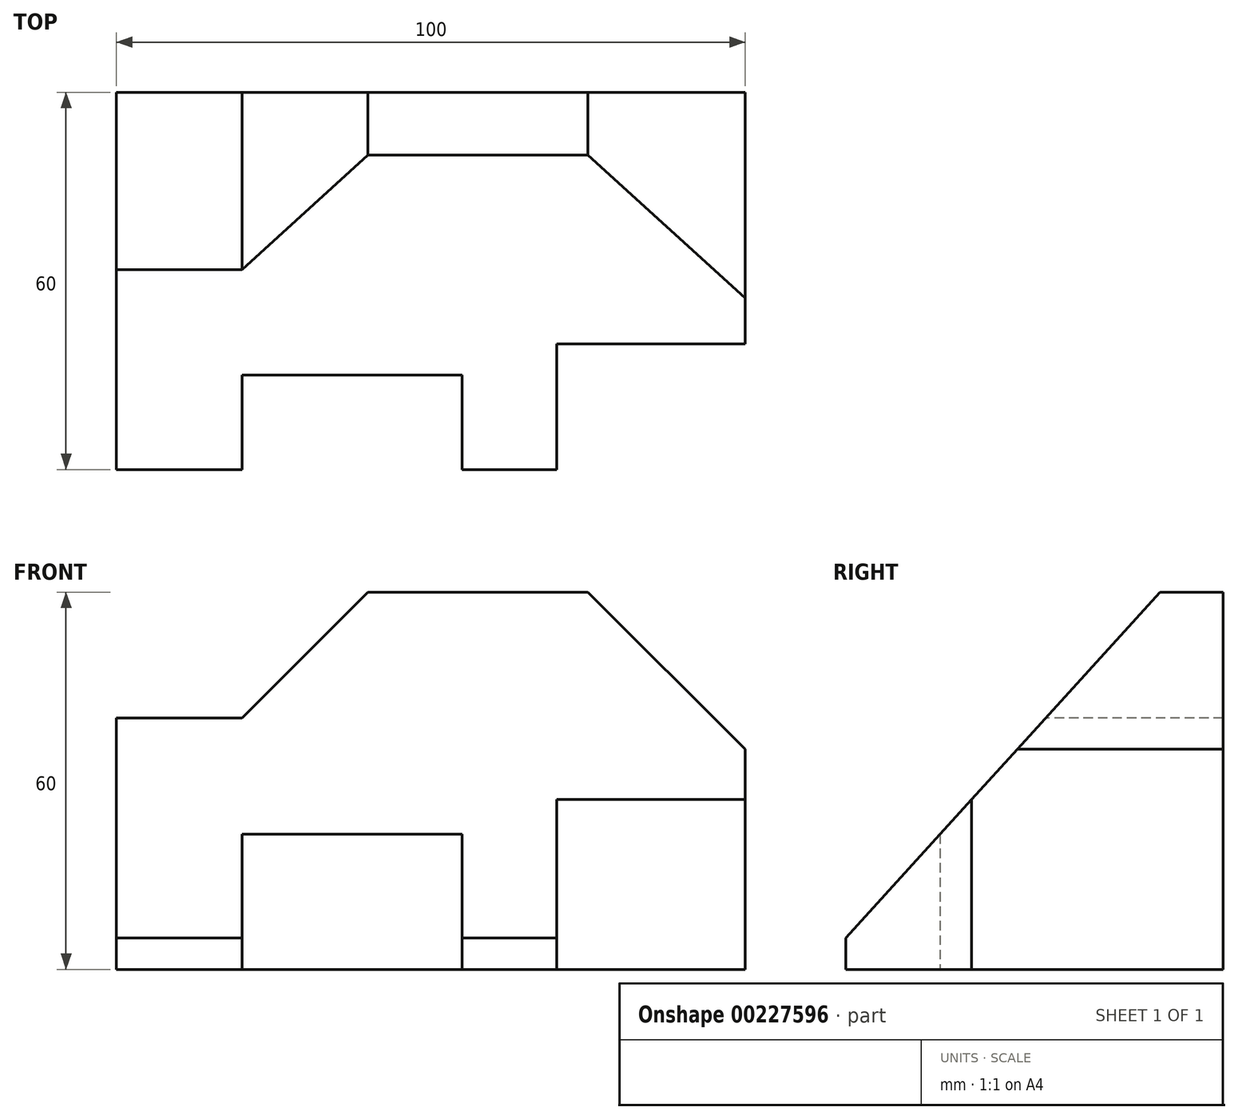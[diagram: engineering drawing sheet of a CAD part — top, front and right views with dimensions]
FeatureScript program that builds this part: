
annotation { "Feature Type Name" : "Feature", "Feature Type Description" : "" }
export const myFeature = defineFeature(function(context is Context, id is Id, definition is map)
    precondition{}
    {
        {
            var Q0;
            Q0=qCreatedBy(makeId("Top.planeOp"),FACE);
            var sketch = newSketch(context, id + "F0", { "sketchPlane" : qUnion([Q0])});
            skLineSegment(sketch, "E0", {"start": v(0, 0) * mm, "end": v(20, 0) * mm});
            skLineSegment(sketch, "E1", {"start": v(20, 0) * mm, "end": v(20, 15) * mm});
            skLineSegment(sketch, "E2", {"start": v(20, 15) * mm, "end": v(55, 15) * mm});
            skLineSegment(sketch, "E3", {"start": v(55, 15) * mm, "end": v(55, 0) * mm});
            skLineSegment(sketch, "E4", {"start": v(55, 0) * mm, "end": v(70, 0) * mm});
            skLineSegment(sketch, "E5", {"start": v(70, 0) * mm, "end": v(70, 20) * mm});
            skLineSegment(sketch, "E6", {"start": v(70, 20) * mm, "end": v(100, 20) * mm});
            skLineSegment(sketch, "E7", {"start": v(100, 20) * mm, "end": v(100, 60) * mm});
            skLineSegment(sketch, "E8", {"start": v(100, 60) * mm, "end": v(0, 60) * mm});
            skLineSegment(sketch, "E9", {"start": v(0, 60) * mm, "end": v(0, 0) * mm});
            skSolve(sketch);
        }
        {
            var Q0;
            Q0=makeQuery(id+"F0.imprint","IMPRINT",FACE,{"disambiguationData":[TD([[makeQuery(id+"F0.imprint","IMPRINT",EDGE,{"derivedFrom":sQuery(id+"F0.wireOp",EDGE,"E1")}),1.0]])]});
            extrude(context, id + "F1", {"entities" : qUnion([Q0]), "depth" : 60 * mm});
        }
        {
            var Q0;
            Q0=qCreatedBy(makeId("Front.planeOp"),FACE);
            var sketch = newSketch(context, id + "F2", { "sketchPlane" : qUnion([Q0])});
            skLineSegment(sketch, "E10.0.0", {"start": v(0, 0) * mm, "end": v(20, 0) * mm, "construction": true});
            skLineSegment(sketch, "E10.0.1", {"start": v(20, 0) * mm, "end": v(20, 60) * mm, "construction": true});
            skLineSegment(sketch, "E10.0.2", {"start": v(20, 60) * mm, "end": v(0, 60) * mm, "construction": true});
            skLineSegment(sketch, "E10.0.3", {"start": v(0, 60) * mm, "end": v(0, 0) * mm, "construction": true});
            skLineSegment(sketch, "E11.0.0", {"start": v(20, 0) * mm, "end": v(55, 0) * mm, "construction": true});
            skLineSegment(sketch, "E11.0.1", {"start": v(55, 0) * mm, "end": v(55, 60) * mm, "construction": true});
            skLineSegment(sketch, "E11.0.2", {"start": v(55, 60) * mm, "end": v(20, 60) * mm, "construction": true});
            skLineSegment(sketch, "E11.0.3", {"start": v(20, 60) * mm, "end": v(20, 0) * mm, "construction": true});
            skLineSegment(sketch, "E12.0.0", {"start": v(55, 0) * mm, "end": v(70, 0) * mm, "construction": true});
            skLineSegment(sketch, "E12.0.1", {"start": v(70, 0) * mm, "end": v(70, 60) * mm, "construction": true});
            skLineSegment(sketch, "E12.0.2", {"start": v(70, 60) * mm, "end": v(55, 60) * mm, "construction": true});
            skLineSegment(sketch, "E12.0.3", {"start": v(55, 60) * mm, "end": v(55, 0) * mm, "construction": true});
            skLineSegment(sketch, "E13.0.0", {"start": v(70, 0) * mm, "end": v(100, 0) * mm, "construction": true});
            skLineSegment(sketch, "E13.0.1", {"start": v(100, 0) * mm, "end": v(100, 60) * mm, "construction": true});
            skLineSegment(sketch, "E13.0.2", {"start": v(100, 60) * mm, "end": v(70, 60) * mm, "construction": true});
            skLineSegment(sketch, "E13.0.3", {"start": v(70, 60) * mm, "end": v(70, 0) * mm, "construction": true});
            skLineSegment(sketch, "E14", {"start": v(0, 40) * mm, "end": v(20, 40) * mm});
            skLineSegment(sketch, "E15", {"start": v(20, 40) * mm, "end": v(40, 60) * mm});
            skLineSegment(sketch, "E16", {"start": v(40, 60) * mm, "end": v(75, 60) * mm});
            skLineSegment(sketch, "E17", {"start": v(75, 60) * mm, "end": v(100, 35) * mm});
            skLineSegment(sketch, "E18", {"start": v(0, 40) * mm, "end": v(0, 60) * mm});
            skLineSegment(sketch, "E19", {"start": v(75, 60) * mm, "end": v(100, 60) * mm});
            skLineSegment(sketch, "E20", {"start": v(100, 60) * mm, "end": v(100, 35) * mm});
            skLineSegment(sketch, "E21", {"start": v(40, 60) * mm, "end": v(0, 60) * mm});
            skLineSegment(sketch, "E22", {"start": v(0, 60) * mm, "end": v(0, 40) * mm});
            skSolve(sketch);
        }
        {
            var Q0;
            Q0=makeQuery(id+"F2.imprint","IMPRINT",FACE,{"disambiguationData":[TD([[makeQuery(id+"F2.imprint","IMPRINT",EDGE,{"derivedFrom":sQuery(id+"F2.wireOp",EDGE,"E14")}),1.0]])]});
            var Q1;
            Q1=makeQuery(id+"F2.imprint","IMPRINT",FACE,{"disambiguationData":[TD([[makeQuery(id+"F2.imprint","IMPRINT",EDGE,{"derivedFrom":sQuery(id+"F2.wireOp",EDGE,"E17")}),1.0]])]});
            extrude(context, id + "F3", {"entities" : qUnion([Q0, Q1]), "operationType" : NewBodyOperationType.REMOVE, "endBound" : BoundingType.THROUGH_ALL, "oppositeDirection" : true, "depth" : 25 * mm});
        }
        {
            var Q0;
            Q0=makeQuery(id+"F1.opExtrude","SWEPT_FACE",FACE,{"disambiguationData":[OSD([sQuery(id+"F0.wireOp",EDGE,"E7")])]});
            var sketch = newSketch(context, id + "F4", { "sketchPlane" : qUnion([Q0])});
            skLineSegment(sketch, "E23", {"start": v(50, 60) * mm, "end": v(0, 5) * mm});
            skLineSegment(sketch, "E24.0.0", {"start": v(0, 0) * mm, "end": v(20, 0) * mm});
            skLineSegment(sketch, "E24.0.3", {"start": v(0, 60) * mm, "end": v(0, 0) * mm});
            skLineSegment(sketch, "E25.0", {"start": v(60, 60) * mm, "end": v(20, 60) * mm, "construction": true});
            skLineSegment(sketch, "E26.0.3", {"start": v(0, 60) * mm, "end": v(0, 0) * mm, "construction": true});
            skLineSegment(sketch, "E27", {"start": v(50, 60) * mm, "end": v(0, 60) * mm});
            skLineSegment(sketch, "E28", {"start": v(0, 5) * mm, "end": v(0, 60) * mm});
            skSolve(sketch);
        }
        {
            var Q0;
            Q0 = qSketchRegion(id + "F4", true);
            extrude(context, id + "F5", {"entities" : qUnion([Q0]), "operationType" : NewBodyOperationType.REMOVE, "endBound" : BoundingType.THROUGH_ALL, "oppositeDirection" : true, "depth" : 25 * mm});
        }
    });
